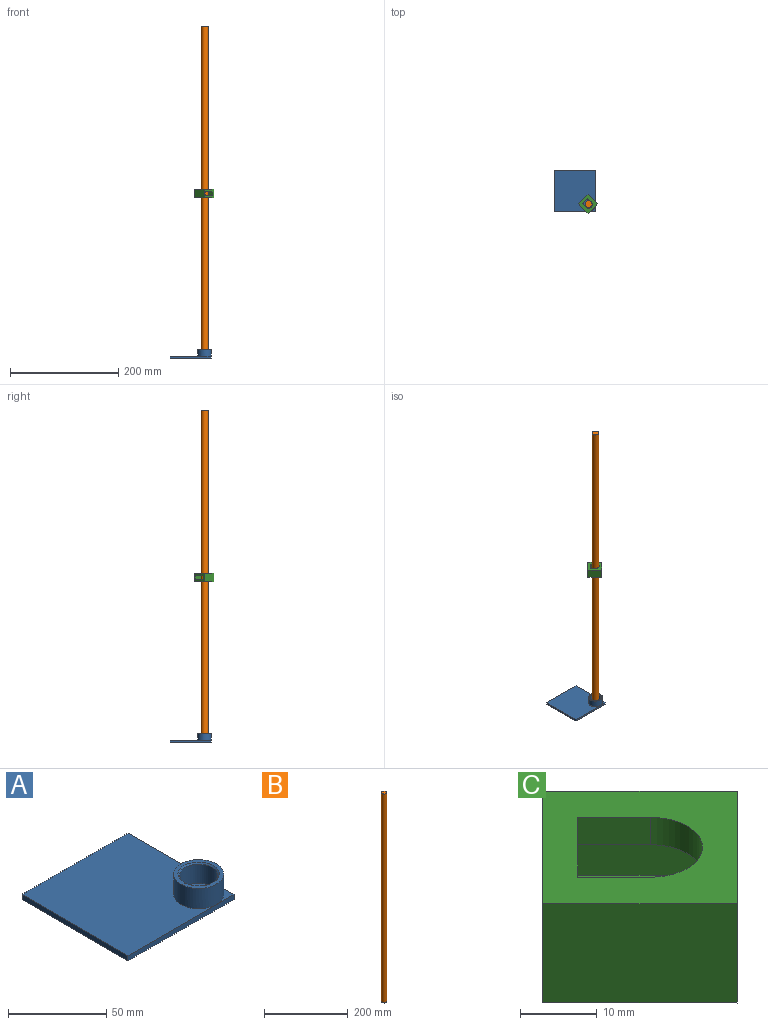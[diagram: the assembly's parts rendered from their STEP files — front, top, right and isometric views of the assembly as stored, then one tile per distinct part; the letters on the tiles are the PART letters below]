
ASSEMBLY  parts=3 mates=2
PART A: 12 faces, bbox 76.2x76.2x15.9 mm
  f0: plane 76.2x76.2mm, normal (0,0,1), area 5265.1mm2, adj f1,f2,f3,f4,f8
  f1: plane 76.2x3.18mm, normal (1,0,0), area 241.9mm2, adj f0,f2,f4,f5,f6
  f2: plane 76.2x3.18mm, normal (0,1,0), area 241.9mm2, adj f0,f1,f3,f6
  f3: plane 76.2x3.18mm, normal (-1,0,0), area 241.9mm2, adj f0,f2,f4,f6
  f4: plane 76.2x3.18mm, normal (0,-1,0), area 241.9mm2, adj f0,f1,f3,f5,f6
  f5: plane 12.7x12.7mm, normal (0,0,1), area 34.6mm2, adj f1,f4,f8
  f6: plane 76.2x76.2mm, normal (0,0,-1), area 5806.4mm2, adj f1,f2,f3,f4
  f7: cylinder r=9.72mm len=19.45mm, axis (0,0,-1), area 727.4mm2, adj f10,f11
  f8: cylinder r=12.7mm len=25.4mm, axis (0,0,-1), area 1013.4mm2, adj f0,f5,f9
  f9: plane 25.4x25.4mm, normal (0,0,1), area 159.2mm2, adj f8,f11
  f10: plane 19.45x19.45mm, normal (0,0,1), area 297mm2, adj f7
  f11: cone r=9.72mm half-angle=45deg, axis (0,0,1), area 71.4mm2, adj f7,f9
PART B: 3 faces, bbox 12.7x12.7x609.6 mm
  f0: cylinder r=6.35mm len=609.6mm, axis (0,0,-1), area 24322mm2, adj f1,f2
  f1: plane 12.7x12.7mm, normal (0,0,1), area 126.7mm2, adj f0
  f2: plane 12.7x12.7mm, normal (0,0,-1), area 126.7mm2, adj f0
PART C: 18 faces, bbox 35.9x35.9x15.9 mm
  f0: plane 17.96x17.96mm, normal (0.71,-0.71,0), area 261.5mm2, adj f6,f7,f12,f13,f14,f15,f16,f17
  f1: cylinder r=6.75mm len=11.52mm, axis (0,0,1), area 92.5mm2, adj f2,f4,f13,f14
  f2: plane 6.74x6.74mm, normal (0.71,0.71,0), area 41.6mm2, adj f1,f3,f13,f14
  f3: plane 9.54x9.54mm, normal (0.71,-0.71,0), area 58.9mm2, adj f2,f4,f13,f14
  f4: plane 6.74x6.74mm, normal (-0.71,-0.71,0), area 41.6mm2, adj f1,f3,f13,f14
  f5: plane 17.96x17.96mm, normal (-0.71,0.71,0), area 261.5mm2, adj f6,f7,f12,f13,f14,f15,f16,f17
  f6: plane 17.96x17.96mm, normal (-0.71,-0.71,0), area 403.2mm2, adj f0,f5,f12,f13
  f7: plane 17.96x17.96mm, normal (0.71,0.71,0), area 403.2mm2, adj f0,f5,f12,f13
  f8: cylinder r=6.75mm len=11.52mm, axis (0,0,1), area 92.5mm2, adj f9,f11,f12,f15
  f9: plane 6.74x6.74mm, normal (0.71,0.71,0), area 41.6mm2, adj f8,f10,f12,f15
  f10: plane 9.54x9.54mm, normal (0.71,-0.71,0), area 58.9mm2, adj f9,f11,f12,f15
  f11: plane 6.74x6.74mm, normal (-0.71,-0.71,0), area 41.6mm2, adj f8,f10,f12,f15
  f12: plane 35.92x35.92mm, normal (0,0,-1), area 445.1mm2, adj f0,f5,f6,f7,f8,f9,f10,f11
  f13: plane 35.92x35.92mm, normal (0,0,1), area 445.1mm2, adj f0,f1,f2,f3,f4,f5,f6,f7
  f14: plane 31.99x31.99mm, normal (0,0,-1), area 304mm2, adj f0,f1,f2,f3,f4,f5,f16,f17
  f15: plane 31.99x31.99mm, normal (0,0,1), area 304mm2, adj f0,f5,f8,f9,f10,f11,f16,f17
  f16: plane 17.96x17.96mm, normal (-0.71,-0.71,0), area 181.5mm2, adj f0,f5,f14,f15
  f17: plane 17.96x17.96mm, normal (0.71,0.71,0), area 181.5mm2, adj f0,f5,f14,f15
PLACE A t=(-3.16,0.54,3.74)mm
PLACE B t=(-3.16,0.54,6.92)mm
PLACE C t=(-3.16,0.54,315.15)mm
MATE fastened A.f7 <-> B.f0  axis (0,0,1) through (-3.16,0.54,6.92)mm
MATE slider C.f1 <-> B.f0  axis (0,0,1) through (-3.16,0.54,312.97)mm
